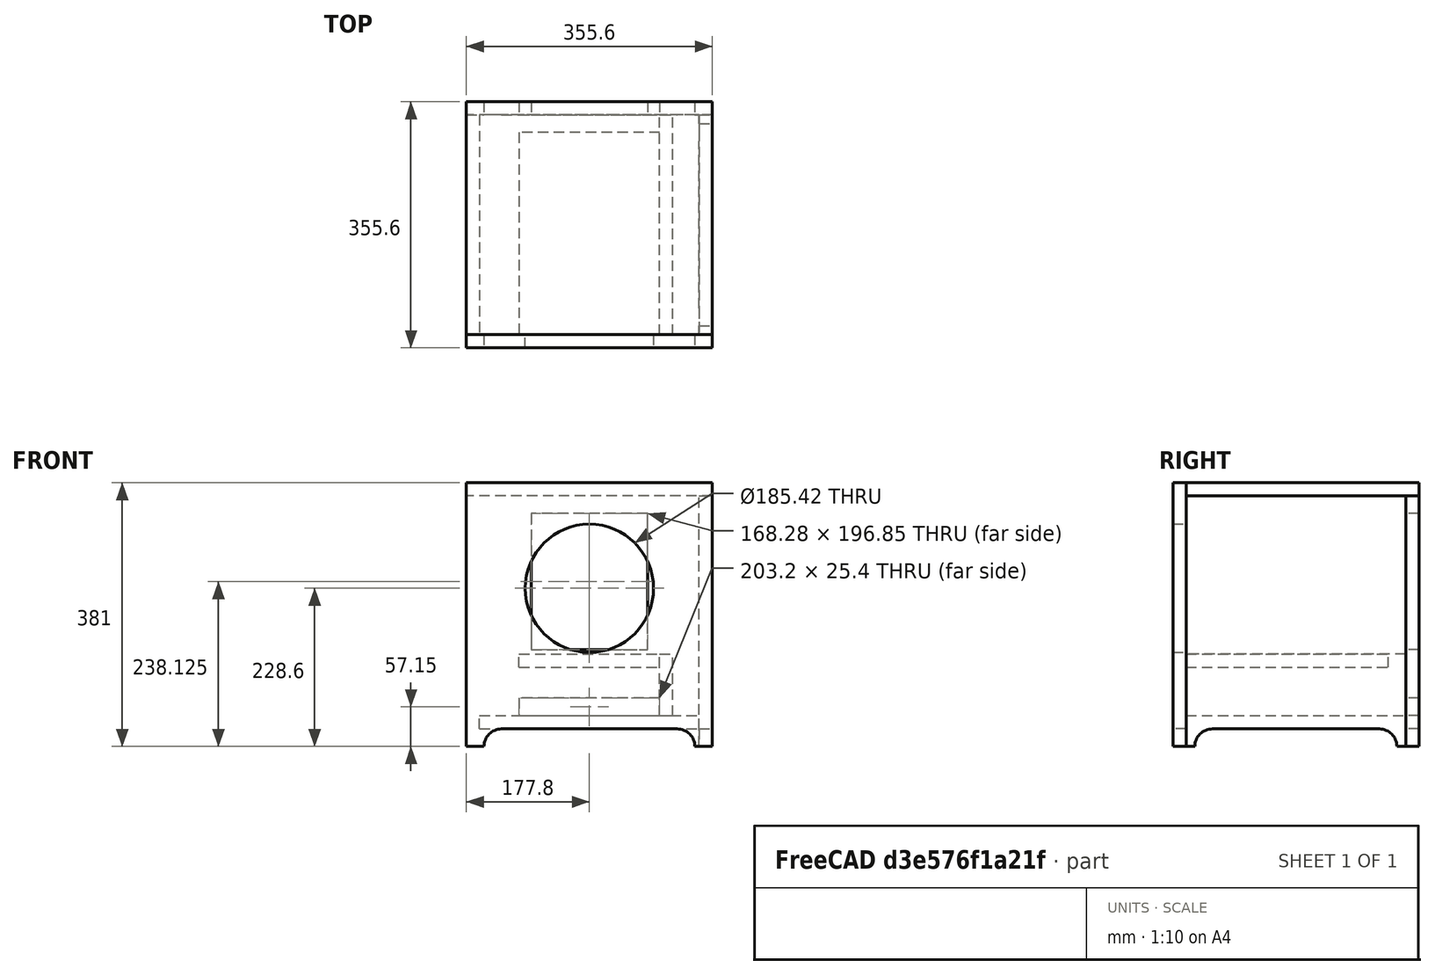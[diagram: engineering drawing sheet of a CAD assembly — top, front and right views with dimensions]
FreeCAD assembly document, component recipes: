
FREECAD ASSEMBLY — COMPONENT RECIPES ("Turtle 2 Subwoofer")

This assembly document has 10 components, labeled P0..P9 below (a component is one placed body or linked part). 10 of them carry a construction recipe — the FreeCAD feature program that regenerates the part from scratch, quoted from this document or its linked companion documents; the rest are supplied as boundary geometry only. No exploded tour is included for this assembly.
COMPONENT P0 — recipe-attached ("Front", modeled in this document).
Construction recipe (the document's own serialized feature program — sketch geometry with constraints, then the solid features built on it; lengths are millimeters unless a unit is written):

FEATURE [Sketcher::SketchObject] Sketch
  ArcFitTolerance = 1e-06
  AttachmentSupport = -> [XZ_Plane001]
  FullyConstrained = true
  MakeInternals = false
  MapMode = 5
  Placement = pos=(0,0,0) rot=(1,0,0;1.5708rad)
  sketch-geometry (17):
    g0: LineSegment [constr] StartX=0 StartY=0 StartZ=0 EndX=355.6 EndY=0 EndZ=0
    g1: LineSegment StartX=355.6 StartY=0 StartZ=0 EndX=355.6 EndY=381 EndZ=0
    g2: LineSegment StartX=355.6 StartY=381 StartZ=0 EndX=0 EndY=381 EndZ=0
    g3: LineSegment StartX=0 StartY=381 StartZ=0 EndX=0 EndY=0 EndZ=0
    g4: GeomPoint X=177.8 Y=0 Z=0
    g5: LineSegment [constr] StartX=177.8 StartY=0 StartZ=0 EndX=177.8 EndY=25.4 EndZ=0
    g6: LineSegment StartX=0 StartY=0 StartZ=0 EndX=25.4 EndY=3.1e-15 EndZ=0
    g7: LineSegment StartX=330.2 StartY=0 StartZ=0 EndX=355.6 EndY=0 EndZ=0
    g8: GeomPoint X=50.8 Y=0 Z=0
    g9: GeomPoint [constr] X=304.8 Y=0 Z=0
    g10: LineSegment [constr] StartX=0 StartY=25.4 StartZ=0 EndX=355.6 EndY=25.4 EndZ=0
    g11: LineSegment [constr] StartX=50.8 StartY=0 StartZ=0 EndX=50.8 EndY=25.4 EndZ=0
    g12: ArcOfCircle CenterX=50.8 CenterY=0 CenterZ=0 NormalX=0 NormalY=0 NormalZ=1 AngleXU=0 Radius=25.4 StartAngle=1.5708 EndAngle=3.14159
    g13: ArcOfCircle CenterX=304.8 CenterY=3.4e-15 CenterZ=0 NormalX=0 NormalY=0 NormalZ=1 AngleXU=0 Radius=25.4 StartAngle=0 EndAngle=1.5708
    g14: LineSegment StartX=50.8 StartY=25.4 StartZ=0 EndX=304.8 EndY=25.4 EndZ=0
    g15: LineSegment [constr] StartX=177.8 StartY=0 StartZ=0 EndX=177.8 EndY=381 EndZ=0
    g16: Circle CenterX=177.8 CenterY=228.6 CenterZ=0 NormalX=0 NormalY=0 NormalZ=1 AngleXU=0 Radius=92.71
  constraints (44):
    c: Coincident(g0,g1)
    c: Coincident(g1,g2)
    c: Coincident(g2,g3)
    c: Coincident(g3,g0)
    c: Horizontal(g0)
    c: Horizontal(g2)
    c: Vertical(g1)
    c: Vertical(g3)
    c: DistanceX(g2,g2) = 355.6
    c: DistanceY(g1,g1) = 381
    c: Coincident(g0,g-1)
    c: PointOnObject(g6,g0)
    c: Symmetric(g0,g0,g4)
    c: Coincident(g5,g4)
    c: Coincident(g6,g0)
    c: Coincident(g7,g0)
    c: Horizontal(g7)
    c: Symmetric(g6,g7,g5)
    c: DistanceX(g7,g7) = 25.4
    c: PointOnObject(g8,g0)
    c: DistanceX(g6,g8) = 25.4
    c: PointOnObject(g9,g0)
    c: DistanceX(g9,g7) = 25.4
    c: PointOnObject(g10,g3)
    c: PointOnObject(g10,g1)
    c: Horizontal(g10)
    c: Distance(g0,g10) = 25.4
    c: PointOnObject(g5,g10)
    c: Coincident(g11,g8)
    c: PointOnObject(g11,g10)
    c: Coincident(g12,g6)
    c: Coincident(g12,g11)
    c: Coincident(g8,g12)
    c: Equal(g12,g13)
    c: Symmetric(g12,g13,g5)
    c: Symmetric(g12,g13,g5)
    c: Coincident(g14,g11)
    c: Coincident(g14,g13)
    c: Coincident(g15,g4)
    c: Symmetric(g2,g2,g15)
    c: Diameter(g16) = 185.42
    c: PointOnObject(g16,g15)
    c: DistanceY(g16,g15) = 152.4
    c: DistanceY(g5,g16) = 203.2
FEATURE [PartDesign::Pad] Pad
  Direction = (0,-1,2e-16)
  Length = 19.05
  Length2 = 10
  Placement = pos=(0,0,0) rot=(1,0,0;1.5708rad)
  Profile = -> Sketch
  ReferenceAxis = -> Sketch [N_Axis]
  Suppressed = false
  Type = 0
FEATURE [PartDesign::Body] Body  label="Front"
  AllowCompound = false
  Group = -> [Sketch,Pad]
  Origin = -> Origin001
  Tip = -> Pad
COMPONENT P1 — recipe-attached ("Rear", modeled in this document).
Construction recipe (the document's own serialized feature program — sketch geometry with constraints, then the solid features built on it; lengths are millimeters unless a unit is written):

FEATURE [Sketcher::SketchObject] Sketch001
  ArcFitTolerance = 1e-06
  AttachmentSupport = -> [XZ_Plane002]
  FullyConstrained = true
  MakeInternals = false
  MapMode = 5
  Placement = pos=(0,0,0) rot=(1,0,0;1.5708rad)
  sketch-geometry (28):
    g0: LineSegment [constr] StartX=0 StartY=0 StartZ=0 EndX=355.6 EndY=0 EndZ=0
    g1: LineSegment StartX=355.6 StartY=0 StartZ=0 EndX=355.6 EndY=361.95 EndZ=0
    g2: LineSegment StartX=355.6 StartY=361.95 StartZ=0 EndX=0 EndY=361.95 EndZ=0
    g3: LineSegment StartX=0 StartY=361.95 StartZ=0 EndX=0 EndY=0 EndZ=0
    g4: GeomPoint X=177.8 Y=0 Z=0
    g5: LineSegment [constr] StartX=177.8 StartY=0 StartZ=0 EndX=177.8 EndY=25.4 EndZ=0
    g6: LineSegment StartX=0 StartY=0 StartZ=0 EndX=25.4 EndY=3.1e-15 EndZ=0
    g7: LineSegment StartX=330.2 StartY=0 StartZ=0 EndX=355.6 EndY=0 EndZ=0
    g8: GeomPoint X=50.8 Y=0 Z=0
    g9: GeomPoint [constr] X=304.8 Y=0 Z=0
    g10: LineSegment [constr] StartX=0 StartY=25.4 StartZ=0 EndX=355.6 EndY=25.4 EndZ=0
    g11: LineSegment [constr] StartX=50.8 StartY=0 StartZ=0 EndX=50.8001 EndY=25.4 EndZ=0
    g12: ArcOfCircle CenterX=50.8 CenterY=0 CenterZ=0 NormalX=0 NormalY=0 NormalZ=1 AngleXU=0 Radius=25.4 StartAngle=1.57079 EndAngle=3.14159
    g13: ArcOfCircle CenterX=304.8 CenterY=1.3e-15 CenterZ=0 NormalX=0 NormalY=0 NormalZ=1 AngleXU=0 Radius=25.4 StartAngle=0 EndAngle=1.5708
    g14: LineSegment StartX=50.8001 StartY=25.4 StartZ=0 EndX=304.8 EndY=25.4 EndZ=0
    g15: LineSegment [constr] StartX=0 StartY=44.45 StartZ=0 EndX=355.6 EndY=44.45 EndZ=0
    g16: LineSegment [constr] StartX=0 StartY=69.85 StartZ=0 EndX=355.6 EndY=69.85 EndZ=0
    g17: LineSegment [constr] StartX=76.2 StartY=0 StartZ=0 EndX=76.2 EndY=69.85 EndZ=0
    g18: LineSegment StartX=76.2 StartY=69.85 StartZ=0 EndX=76.2 EndY=44.45 EndZ=0
    g19: LineSegment StartX=76.2 StartY=44.45 StartZ=0 EndX=279.4 EndY=44.45 EndZ=0
    g20: LineSegment StartX=279.4 StartY=44.45 StartZ=0 EndX=279.4 EndY=69.85 EndZ=0
    g21: LineSegment StartX=279.4 StartY=69.85 StartZ=0 EndX=76.2 EndY=69.85 EndZ=0
    g22: LineSegment [constr] StartX=177.8 StartY=0 StartZ=0 EndX=177.8 EndY=361.95 EndZ=0
    g23: LineSegment StartX=93.6625 StartY=139.7 StartZ=0 EndX=261.938 EndY=139.7 EndZ=0
    g24: LineSegment StartX=261.938 StartY=139.7 StartZ=0 EndX=261.938 EndY=336.55 EndZ=0
    g25: LineSegment StartX=261.938 StartY=336.55 StartZ=0 EndX=93.6625 EndY=336.55 EndZ=0
    g26: LineSegment StartX=93.6625 StartY=336.55 StartZ=0 EndX=93.6625 EndY=139.7 EndZ=0
    g27: GeomPoint X=177.8 Y=238.125 Z=0
  constraints (76):
    c: Coincident(g0,g1)
    c: Coincident(g1,g2)
    c: Coincident(g2,g3)
    c: Coincident(g3,g0)
    c: Horizontal(g0)
    c: Horizontal(g2)
    c: Vertical(g1)
    c: Vertical(g3)
    c: DistanceX(g2,g2) = 355.6
    c: DistanceY(g1,g1) = 361.95
    c: Coincident(g0,g-1)
    c: PointOnObject(g6,g0)
    c: Symmetric(g0,g0,g4)
    c: Coincident(g5,g4)
    c: Coincident(g6,g0)
    c: Coincident(g7,g0)
    c: Horizontal(g7)
    c: Symmetric(g6,g7,g5)
    c: DistanceX(g7,g7) = 25.4
    c: PointOnObject(g8,g0)
    c: DistanceX(g6,g8) = 25.4
    c: PointOnObject(g9,g0)
    c: DistanceX(g9,g7) = 25.4
    c: PointOnObject(g10,g3)
    c: PointOnObject(g10,g1)
    c: Horizontal(g10)
    c: Distance(g0,g10) = 25.4
    c: PointOnObject(g5,g10)
    c: Coincident(g11,g8)
    c: PointOnObject(g11,g10)
    c: Coincident(g12,g6)
    c: Coincident(g12,g11)
    c: Coincident(g8,g12)
    c: Equal(g12,g13)
    c: Symmetric(g12,g13,g5)
    c: Symmetric(g12,g13,g5)
    c: Coincident(g14,g11)
    c: Coincident(g14,g13)
    c: PointOnObject(g15,g3)
    c: PointOnObject(g15,g1)
    c: Horizontal(g15)
    c: Distance(g15,g14) = 19.05
    c: PointOnObject(g16,g3)
    c: PointOnObject(g16,g1)
    c: Horizontal(g16)
    c: Distance(g15,g16) = 25.4
    c: PointOnObject(g17,g0)
    c: PointOnObject(g17,g16)
    c: Vertical(g17)
    c: Distance(g3,g17) = 76.2
    c: Coincident(g18,g19)
    c: Coincident(g19,g20)
    c: Coincident(g20,g21)
    c: Coincident(g21,g18)
    c: Vertical(g18)
    c: Vertical(g20)
    c: Horizontal(g19)
    c: Horizontal(g21)
    c: Coincident(g18,g17)
    c: PointOnObject(g19,g15)
    c: DistanceX(g21,g21) = 203.2
    c: Coincident(g22,g4)
    c: Symmetric(g2,g2,g22)
    c: Coincident(g23,g24)
    c: Coincident(g24,g25)
    c: Coincident(g25,g26)
    c: Coincident(g26,g23)
    c: Horizontal(g23)
    c: Horizontal(g25)
    c: Vertical(g24)
    c: Vertical(g26)
    c: Symmetric(g25,g23,g27)
    c: Distance(g24,g26) = 168.275
    c: Distance(g23,g25) = 196.85
    c: PointOnObject(g27,g22)
    c: Distance(g2,g25) = 25.4
FEATURE [PartDesign::Pad] Pad001
  Direction = (0,-1,2e-16)
  Length = 19.05
  Length2 = 10
  Placement = pos=(0,0,0) rot=(1,0,0;1.5708rad)
  Profile = -> Sketch001
  ReferenceAxis = -> Sketch001 [N_Axis]
  Suppressed = false
  Type = 0
FEATURE [PartDesign::Body] Body001  label="Rear"
  AllowCompound = false
  Group = -> [Sketch001,Pad001]
  Origin = -> Origin002
  Placement = pos=(0,336.55,0) rot=(0,0,1;0rad)
  Tip = -> Pad001
COMPONENT P2 — recipe-attached ("left", modeled in this document).
Construction recipe (the document's own serialized feature program — sketch geometry with constraints, then the solid features built on it; lengths are millimeters unless a unit is written):

FEATURE [Sketcher::SketchObject] Sketch002
  ArcFitTolerance = 1e-06
  AttachmentSupport = -> [XZ_Plane003]
  FullyConstrained = true
  MakeInternals = false
  MapMode = 5
  Placement = pos=(0,0,0) rot=(1,0,0;1.5708rad)
  sketch-geometry (15):
    g0: LineSegment [constr] StartX=0 StartY=0 StartZ=0 EndX=317.5 EndY=0 EndZ=0
    g1: LineSegment StartX=317.5 StartY=0 StartZ=0 EndX=317.5 EndY=361.95 EndZ=0
    g2: LineSegment StartX=317.5 StartY=361.95 StartZ=0 EndX=0 EndY=361.95 EndZ=0
    g3: LineSegment StartX=0 StartY=361.95 StartZ=0 EndX=0 EndY=0 EndZ=0
    g4: GeomPoint X=158.75 Y=0 Z=0
    g5: LineSegment [constr] StartX=158.75 StartY=0 StartZ=0 EndX=158.75 EndY=25.4 EndZ=0
    g6: LineSegment StartX=0 StartY=0 StartZ=0 EndX=12.7 EndY=3.1e-15 EndZ=0
    g7: LineSegment StartX=304.8 StartY=0 StartZ=0 EndX=317.5 EndY=0 EndZ=0
    g8: GeomPoint X=38.1 Y=0 Z=0
    g9: GeomPoint [constr] X=279.4 Y=0 Z=0
    g10: LineSegment [constr] StartX=0 StartY=25.4 StartZ=0 EndX=317.5 EndY=25.4 EndZ=0
    g11: LineSegment [constr] StartX=38.1 StartY=0 StartZ=0 EndX=38.0999 EndY=25.4 EndZ=0
    g12: ArcOfCircle CenterX=38.1 CenterY=0 CenterZ=0 NormalX=0 NormalY=0 NormalZ=1 AngleXU=0 Radius=25.4 StartAngle=1.5708 EndAngle=3.14159
    g13: ArcOfCircle CenterX=279.4 CenterY=-4e-16 CenterZ=0 NormalX=0 NormalY=0 NormalZ=1 AngleXU=0 Radius=25.4 StartAngle=0 EndAngle=1.57079
    g14: LineSegment StartX=38.0999 StartY=25.4 StartZ=0 EndX=279.4 EndY=25.4 EndZ=0
  constraints (38):
    c: Coincident(g0,g1)
    c: Coincident(g1,g2)
    c: Coincident(g2,g3)
    c: Coincident(g3,g0)
    c: Horizontal(g0)
    c: Horizontal(g2)
    c: Vertical(g1)
    c: Vertical(g3)
    c: DistanceX(g2,g2) = 317.5
    c: DistanceY(g1,g1) = 361.95
    c: Coincident(g0,g-1)
    c: PointOnObject(g6,g0)
    c: Symmetric(g0,g0,g4)
    c: Coincident(g5,g4)
    c: Coincident(g6,g0)
    c: Coincident(g7,g0)
    c: Horizontal(g7)
    c: Symmetric(g6,g7,g5)
    c: DistanceX(g7,g7) = 12.7
    c: PointOnObject(g8,g0)
    c: DistanceX(g6,g8) = 25.4
    c: PointOnObject(g9,g0)
    c: DistanceX(g9,g7) = 25.4
    c: PointOnObject(g10,g3)
    c: PointOnObject(g10,g1)
    c: Horizontal(g10)
    c: Distance(g0,g10) = 25.4
    c: PointOnObject(g5,g10)
    c: Coincident(g11,g8)
    c: PointOnObject(g11,g10)
    c: Coincident(g12,g6)
    c: Coincident(g12,g11)
    c: Coincident(g8,g12)
    c: Equal(g12,g13)
    c: Symmetric(g12,g13,g5)
    c: Symmetric(g12,g13,g5)
    c: Coincident(g14,g11)
    c: Coincident(g14,g13)
FEATURE [PartDesign::Pad] Pad002
  Direction = (0,-1,2e-16)
  Length = 19.05
  Length2 = 10
  Placement = pos=(0,0,0) rot=(1,0,0;1.5708rad)
  Profile = -> Sketch002
  ReferenceAxis = -> Sketch002 [N_Axis]
  Suppressed = false
  Type = 0
FEATURE [PartDesign::Body] Body002  label="left"
  AllowCompound = false
  Group = -> [Sketch002,Pad002]
  Origin = -> Origin003
  Placement = pos=(0,0,0) rot=(0,0,1;1.5708rad)
  Tip = -> Pad002
COMPONENT P3 — recipe-attached ("right", modeled in this document).
Construction recipe (the document's own serialized feature program — sketch geometry with constraints, then the solid features built on it; lengths are millimeters unless a unit is written):

FEATURE [PartDesign::FeatureBase] Clone
  BaseFeature = -> Body002
  Placement = pos=(0,0,0) rot=(0,0,1;1.5708rad)
  Suppressed = false
FEATURE [PartDesign::Body] Body003  label="right"
  AllowCompound = false
  Group = -> [Clone]
  Origin = -> Origin004
  Placement = pos=(336.55,0,0) rot=(0,0,1;0rad)
  Tip = -> Clone
COMPONENT P4 — recipe-attached ("top", modeled in this document).
Construction recipe (the document's own serialized feature program — sketch geometry with constraints, then the solid features built on it; lengths are millimeters unless a unit is written):

FEATURE [Sketcher::SketchObject] Sketch003
  ArcFitTolerance = 1e-06
  AttachmentSupport = -> [XY_Plane005]
  FullyConstrained = true
  MakeInternals = false
  MapMode = 5
  sketch-geometry (4):
    g0: LineSegment StartX=0 StartY=0 StartZ=0 EndX=355.6 EndY=0 EndZ=0
    g1: LineSegment StartX=355.6 StartY=0 StartZ=0 EndX=355.6 EndY=336.55 EndZ=0
    g2: LineSegment StartX=355.6 StartY=336.55 StartZ=0 EndX=0 EndY=336.55 EndZ=0
    g3: LineSegment StartX=0 StartY=336.55 StartZ=0 EndX=0 EndY=0 EndZ=0
  constraints (11):
    c: Coincident(g0,g1)
    c: Coincident(g1,g2)
    c: Coincident(g2,g3)
    c: Coincident(g3,g0)
    c: Horizontal(g0)
    c: Horizontal(g2)
    c: Vertical(g1)
    c: Vertical(g3)
    c: Coincident(g0,g-1)
    c: DistanceX(g2,g2) = 355.6
    c: DistanceY(g3,g3) = 336.55
FEATURE [PartDesign::Pad] Pad003
  Direction = (0,0,1)
  Length = 19.05
  Length2 = 10
  Profile = -> Sketch003
  ReferenceAxis = -> Sketch003 [N_Axis]
  Suppressed = false
  Type = 0
FEATURE [PartDesign::Body] Body004  label="top"
  AllowCompound = false
  Group = -> [Sketch003,Pad003]
  Origin = -> Origin005
  Placement = pos=(0,0,361.95) rot=(0,0,1;0rad)
  Tip = -> Pad003
COMPONENT P5 — recipe-attached ("bottom", modeled in this document).
Construction recipe (the document's own serialized feature program — sketch geometry with constraints, then the solid features built on it; lengths are millimeters unless a unit is written):

FEATURE [Sketcher::SketchObject] Sketch004
  ArcFitTolerance = 1e-06
  AttachmentSupport = -> [XY_Plane006]
  FullyConstrained = true
  MakeInternals = false
  MapMode = 5
  sketch-geometry (4):
    g0: LineSegment StartX=0 StartY=0 StartZ=0 EndX=317.5 EndY=0 EndZ=0
    g1: LineSegment StartX=317.5 StartY=0 StartZ=0 EndX=317.5 EndY=317.5 EndZ=0
    g2: LineSegment StartX=317.5 StartY=317.5 StartZ=0 EndX=0 EndY=317.5 EndZ=0
    g3: LineSegment StartX=0 StartY=317.5 StartZ=0 EndX=0 EndY=0 EndZ=0
  constraints (11):
    c: Coincident(g0,g1)
    c: Coincident(g1,g2)
    c: Coincident(g2,g3)
    c: Coincident(g3,g0)
    c: Horizontal(g0)
    c: Horizontal(g2)
    c: Vertical(g1)
    c: Vertical(g3)
    c: DistanceX(g2,g2) = 317.5
    c: DistanceY(g1,g1) = 317.5
    c: Coincident(g-1,g0)
FEATURE [PartDesign::Pad] Pad004
  Direction = (0,0,1)
  Length = 19.05
  Length2 = 10
  Profile = -> Sketch004
  ReferenceAxis = -> Sketch004 [N_Axis]
  Suppressed = false
  Type = 0
FEATURE [PartDesign::Body] Body005  label="bottom"
  AllowCompound = false
  Group = -> [Sketch004,Pad004]
  Origin = -> Origin006
  Placement = pos=(19.05,0,25.4) rot=(0,0,1;0rad)
  Tip = -> Pad004
COMPONENT P6 — recipe-attached ("port-mid", modeled in this document).
Construction recipe (the document's own serialized feature program — sketch geometry with constraints, then the solid features built on it; lengths are millimeters unless a unit is written):

FEATURE [Sketcher::SketchObject] Sketch005
  ArcFitTolerance = 1e-06
  AttachmentSupport = -> [XY_Plane007]
  FullyConstrained = true
  MakeInternals = false
  MapMode = 5
  sketch-geometry (4):
    g0: LineSegment StartX=0 StartY=0 StartZ=0 EndX=203.2 EndY=0 EndZ=0
    g1: LineSegment StartX=203.2 StartY=0 StartZ=0 EndX=203.2 EndY=292.1 EndZ=0
    g2: LineSegment StartX=203.2 StartY=292.1 StartZ=0 EndX=0 EndY=292.1 EndZ=0
    g3: LineSegment StartX=0 StartY=292.1 StartZ=0 EndX=0 EndY=0 EndZ=0
  constraints (11):
    c: Coincident(g0,g1)
    c: Coincident(g1,g2)
    c: Coincident(g2,g3)
    c: Coincident(g3,g0)
    c: Horizontal(g0)
    c: Horizontal(g2)
    c: Vertical(g1)
    c: Vertical(g3)
    c: Coincident(g0,g-1)
    c: DistanceX(g2,g2) = 203.2
    c: DistanceY(g1,g1) = 292.1
FEATURE [PartDesign::Pad] Pad005
  Direction = (0,0,1)
  Length = 19.05
  Length2 = 10
  Profile = -> Sketch005
  ReferenceAxis = -> Sketch005 [N_Axis]
  Suppressed = false
  Type = 0
FEATURE [PartDesign::Body] Body006  label="port-mid"
  AllowCompound = false
  Group = -> [Sketch005,Pad005]
  Origin = -> Origin007
  Placement = pos=(76.2,25.4,69.85) rot=(0,0,1;0rad)
  Tip = -> Pad005
COMPONENT P7 — recipe-attached ("port-top", modeled in this document).
Construction recipe (the document's own serialized feature program — sketch geometry with constraints, then the solid features built on it; lengths are millimeters unless a unit is written):

FEATURE [PartDesign::FeatureBase] Clone001
  BaseFeature = -> Body006
  Placement = pos=(76.2,25.4,69.85) rot=(0,0,1;0rad)
  Suppressed = false
FEATURE [PartDesign::Body] Body007  label="port-top"
  AllowCompound = false
  Group = -> [Clone001]
  Origin = -> Origin008
  Placement = pos=(0,-25.4,44.45) rot=(0,0,1;0rad)
  Tip = -> Clone001
COMPONENT P8 — recipe-attached ("port-left", modeled in this document).
Construction recipe (the document's own serialized feature program — sketch geometry with constraints, then the solid features built on it; lengths are millimeters unless a unit is written):

FEATURE [Sketcher::SketchObject] Sketch006
  ArcFitTolerance = 1e-06
  AttachmentSupport = -> [YZ_Plane009]
  FullyConstrained = true
  MakeInternals = false
  MapMode = 5
  Placement = pos=(0,0,0) rot=(0.57735,0.57735,0.57735;2.0944rad)
  sketch-geometry (4):
    g0: LineSegment StartX=0 StartY=0 StartZ=0 EndX=317.5 EndY=0 EndZ=0
    g1: LineSegment StartX=317.5 StartY=0 StartZ=0 EndX=317.5 EndY=88.9 EndZ=0
    g2: LineSegment StartX=317.5 StartY=88.9 StartZ=0 EndX=0 EndY=88.9 EndZ=0
    g3: LineSegment StartX=0 StartY=88.9 StartZ=0 EndX=0 EndY=0 EndZ=0
  constraints (11):
    c: Coincident(g0,g1)
    c: Coincident(g1,g2)
    c: Coincident(g2,g3)
    c: Coincident(g3,g0)
    c: Horizontal(g0)
    c: Horizontal(g2)
    c: Vertical(g1)
    c: Vertical(g3)
    c: Distance(g1,g3) = 317.5
    c: Distance(g0,g2) = 88.9
    c: Coincident(g0,g-1)
FEATURE [PartDesign::Pad] Pad006
  Direction = (1,0,0)
  Length = 19.05
  Length2 = 10
  Placement = pos=(0,0,0) rot=(1,1,1;2.0944rad)
  Profile = -> Sketch006
  ReferenceAxis = -> Sketch006 [N_Axis]
  Suppressed = false
  Type = 0
FEATURE [PartDesign::Body] Body008  label="port-left"
  AllowCompound = false
  Group = -> [Sketch006,Pad006]
  Origin = -> Origin009
  Placement = pos=(57.15,0,44.45) rot=(0,0,1;0rad)
  Tip = -> Pad006
COMPONENT P9 — recipe-attached ("port-right", modeled in this document).
Construction recipe (the document's own serialized feature program — sketch geometry with constraints, then the solid features built on it; lengths are millimeters unless a unit is written):

FEATURE [PartDesign::FeatureBase] Clone002
  BaseFeature = -> Body008
  Placement = pos=(57.15,0,44.45) rot=(0,0,1;0rad)
  Suppressed = false
FEATURE [PartDesign::Body] Body009  label="port-right"
  AllowCompound = false
  Group = -> [Clone002]
  Origin = -> Origin010
  Placement = pos=(222.25,0,0) rot=(0,0,1;0rad)
  Tip = -> Clone002
PROVENANCE & LICENSES
A FreeCAD (.FCStd) document from a public repository crawl; recipes are the document's own serialized feature recipes (and, for linked parts, companion documents' recipes).
License: as declared in the source repository (recorded in the dataset sidecar).
